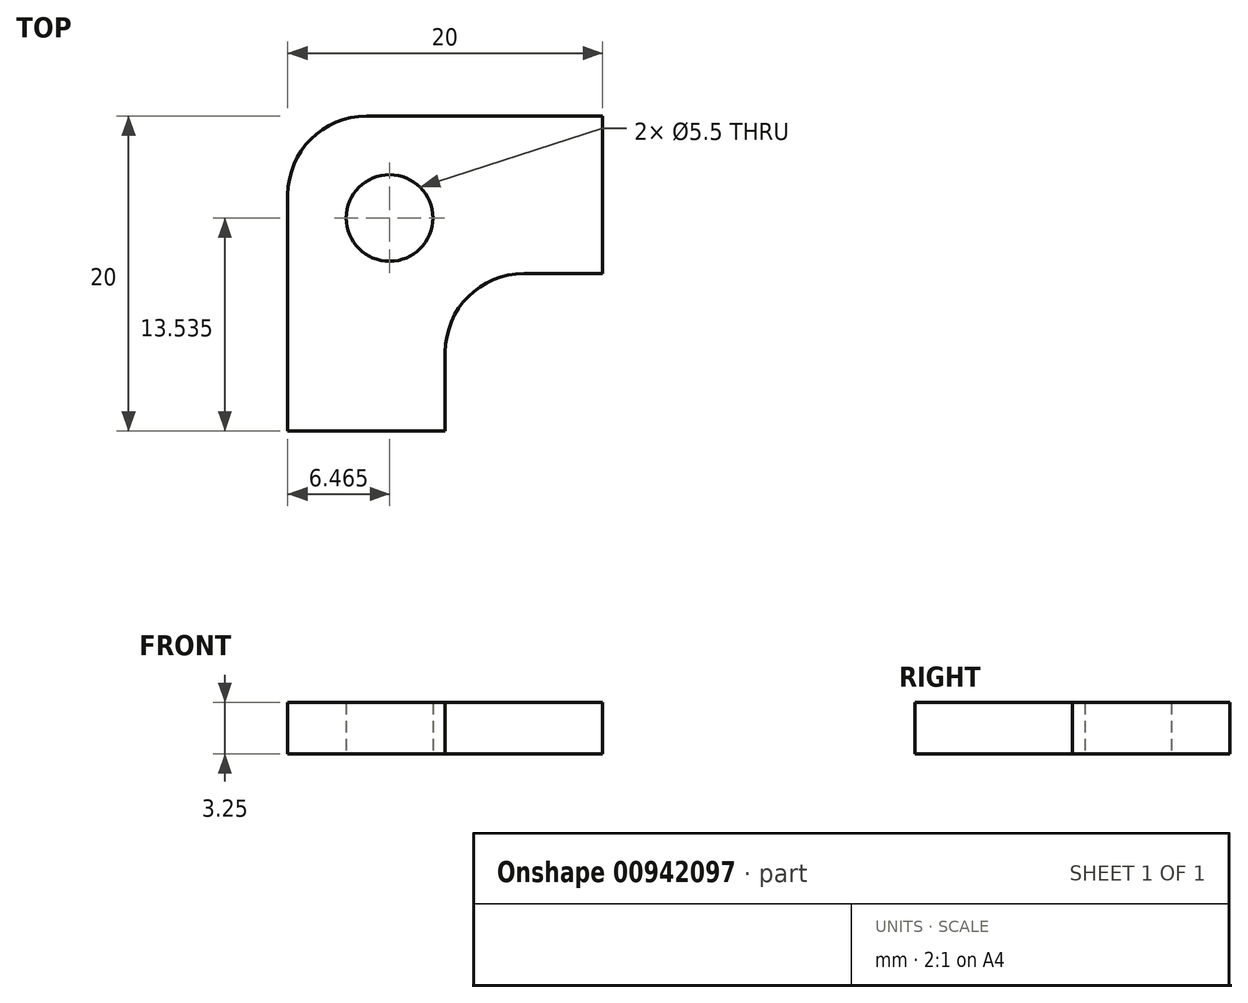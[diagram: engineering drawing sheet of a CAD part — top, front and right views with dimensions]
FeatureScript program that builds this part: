
annotation { "Feature Type Name" : "Feature", "Feature Type Description" : "" }
export const myFeature = defineFeature(function(context is Context, id is Id, definition is map)
    precondition{}
    {
        {
            var Q0;
            Q0=qCreatedBy(makeId("Top.planeOp"),FACE);
            var sketch = newSketch(context, id + "F0", { "sketchPlane" : qUnion([Q0])});
            skLineSegment(sketch, "E0", {"start": v(5, 0) * mm, "end": v(20, 0) * mm});
            skLineSegment(sketch, "E1", {"start": v(0, -5) * mm, "end": v(0, -20) * mm});
            skLineSegment(sketch, "E2.0", {"start": v(15, -10) * mm, "end": v(20, -10) * mm});
            skLineSegment(sketch, "E2.1", {"start": v(10, -15) * mm, "end": v(10, -20) * mm});
            skLineSegment(sketch, "E3", {"start": v(20, 0) * mm, "end": v(20, -10) * mm});
            skLineSegment(sketch, "E4", {"start": v(10, -20) * mm, "end": v(0, -20) * mm});
            skPoint(sketch, "E5.visualSharp", {"position": v(0, 0) * mm});
            skArc(sketch, "E5.filletArc", {"start": v(5, 0) * mm, "mid": v(1.46, -1.46) * mm, "end": v(0, -5) * mm});
            skPoint(sketch, "E6.visualSharp", {"position": v(10, -10) * mm});
            skArc(sketch, "E6.filletArc", {"start": v(15, -10) * mm, "mid": v(11.46, -11.46) * mm, "end": v(10, -15) * mm});
            skLineSegment(sketch, "E7", {"start": v(1.46, -1.46) * mm, "end": v(11.46, -11.46) * mm});
            skCircle(sketch, "E8", {"center": v(6.46, -6.46) * mm, "radius": 2.75 * mm});
            skSolve(sketch);
        }
        {
            var Q0;
            {var subQ1=sQuery(id+"F0.wireOp",EDGE,"E1");Q0=makeQuery(id+"F0.imprint","IMPRINT",FACE,{"disambiguationData":[TD([[makeQuery(id+"F0.imprint","IMPRINT",EDGE,{"derivedFrom":subQ1}),1.0]])]});}
            var Q1;
            {var subQ1=sQuery(id+"F0.wireOp",EDGE,"E0");Q1=makeQuery(id+"F0.imprint","IMPRINT",FACE,{"disambiguationData":[TD([[makeQuery(id+"F0.imprint","IMPRINT",EDGE,{"derivedFrom":subQ1}),-1.0]])]});}
            extrude(context, id + "F1", {"entities" : qUnion([Q0, Q1]), "depth" : 3.25 * mm, "offsetDistance" : 25 * mm});
        }
    });
